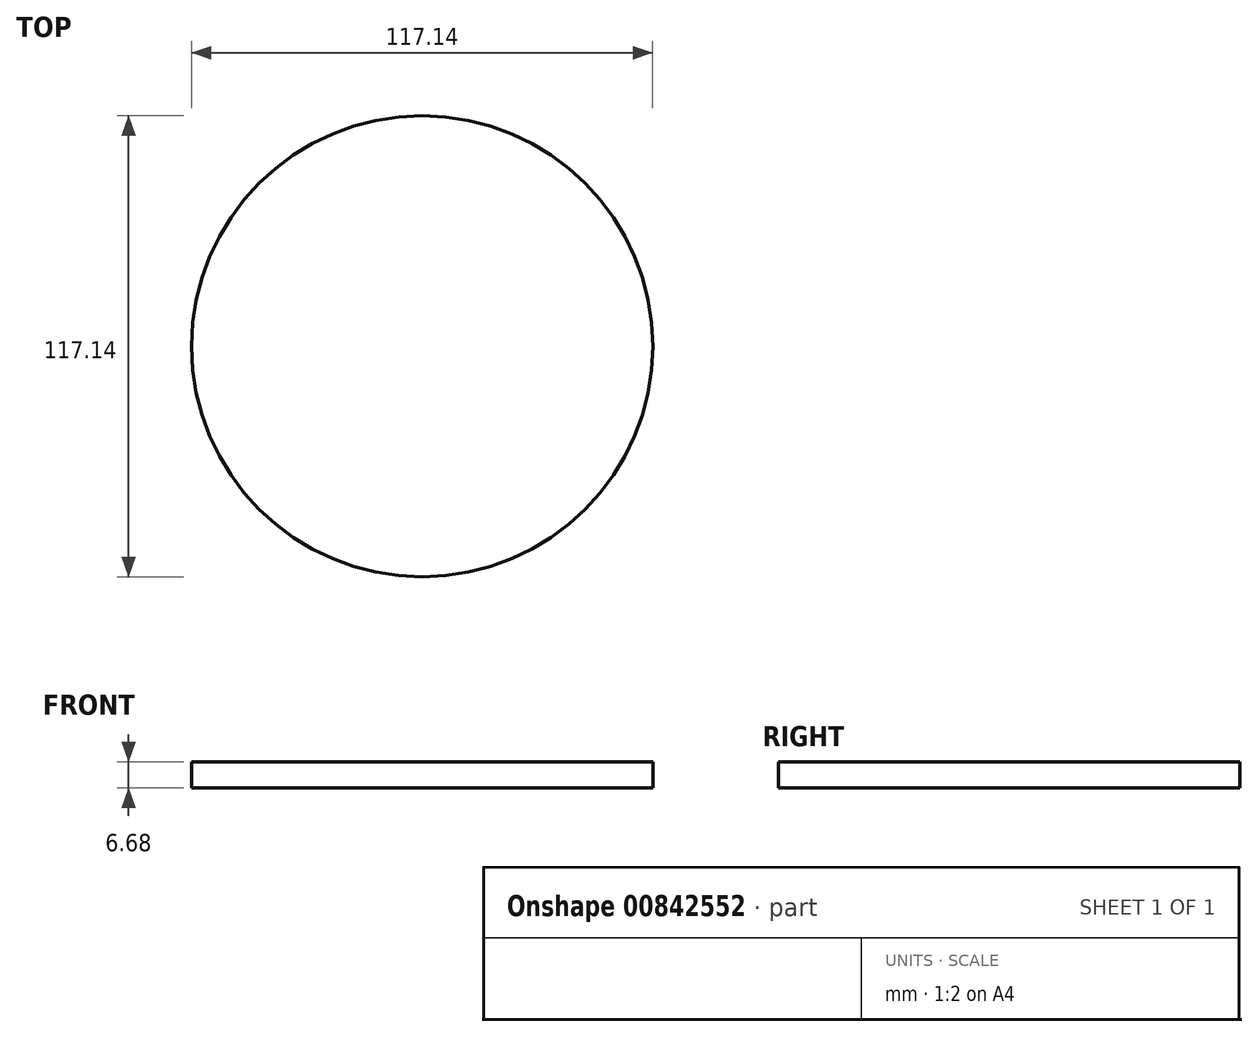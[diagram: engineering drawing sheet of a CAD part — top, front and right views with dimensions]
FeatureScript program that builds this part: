
annotation { "Feature Type Name" : "Feature", "Feature Type Description" : "" }
export const myFeature = defineFeature(function(context is Context, id is Id, definition is map)
    precondition{}
    {
        {
            var Q0;
            Q0=qCreatedBy(makeId("Top.planeOp"),FACE);
            var sketch = newSketch(context, id + "F0", { "sketchPlane" : qUnion([Q0])});
            skCircle(sketch, "E0", {"center": v(0, 0) * mm, "radius": 58.57 * mm});
            skSolve(sketch);
        }
        {
            var Q0;
            Q0=qSketchRegion(id+"F0",true);
            extrude(context, id + "F1", {"entities" : qUnion([Q0]), "depth" : 6.68 * mm, "offsetDistance" : 25.4 * mm});
        }
    });
